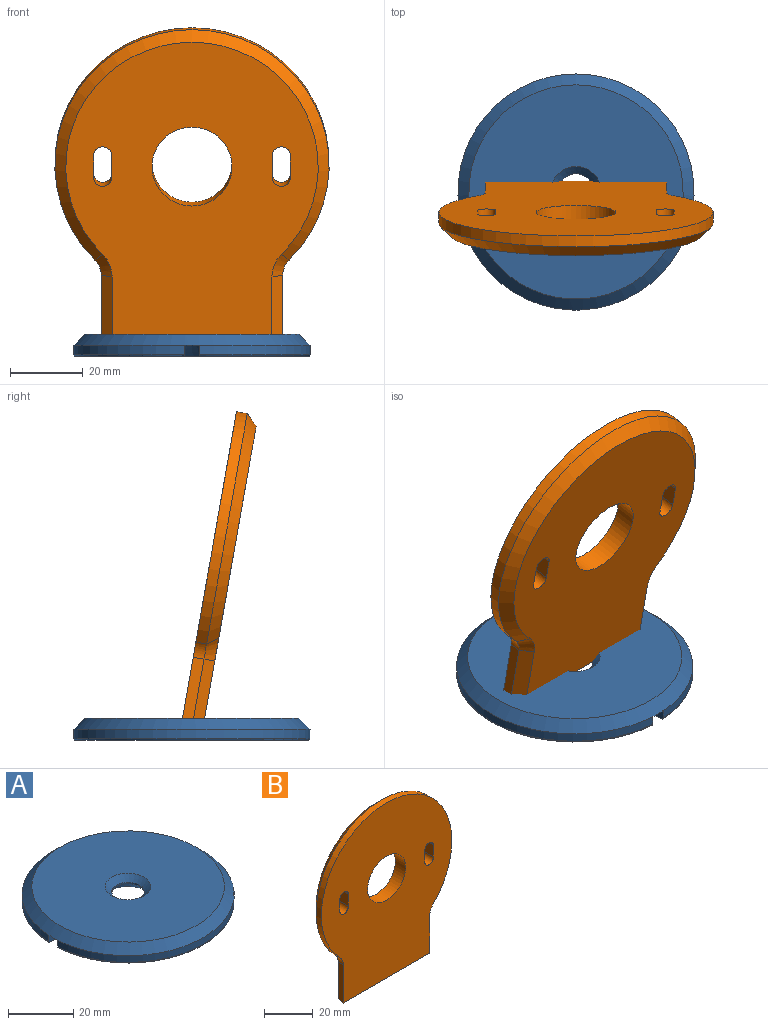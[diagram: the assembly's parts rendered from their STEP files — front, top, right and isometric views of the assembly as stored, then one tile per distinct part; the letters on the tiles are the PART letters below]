
ASSEMBLY  parts=2 mates=1
PART A: 11 faces, bbox 70.5x70.6x6.2 mm
  f0: cylinder r=5mm len=10mm, axis (0,0,-1), area 15.7mm2, adj f8,f9
  f1: plane 64x63.94mm, normal (0,0,-1), area 2895.8mm2, adj f5,f6,f9,f10
  f2: cylinder r=32.5mm len=65mm, axis (0,0,-1), area 500.5mm2, adj f4,f5,f6,f10
  f3: plane 59x59mm, normal (0,0,1), area 2580mm2, adj f4,f8
  f4: cone r=29.5mm half-angle=45deg, axis (0,0,-1), area 826.4mm2, adj f2,f3,f7
  f5: plane 27.52x3.21mm, normal (0,-1,0), area 77.2mm2, adj f1,f2,f7,f9,f10
  f6: plane 27.52x3.21mm, normal (0,1,0), area 77.2mm2, adj f1,f2,f7,f9,f10
  f7: plane 27.38x4mm, normal (0,0,-1), area 108.4mm2, adj f4,f5,f6,f9
  f8: cone r=5mm half-angle=45deg, axis (0,0,1), area 106.6mm2, adj f0,f3
  f9: cone r=8.5mm half-angle=45deg, axis (0,0,-1), area 192.1mm2, adj f0,f1,f5,f6,f7
  f10: torus R=32mm, axis (0,0,1), area 156.3mm2, adj f1,f2,f5,f6
PART B: 22 faces, bbox 75.5x6x87.8 mm
  f0: plane 19.13x3mm, normal (1,0,0), area 56.6mm2, adj f3,f4,f16,f21
  f1: plane 19.13x3mm, normal (-1,0,0), area 56.6mm2, adj f2,f6,f16,f21
  f2: plane 18.6x3mm, normal (-0.71,0.71,0), area 77.8mm2, adj f1,f17,f18,f21
  f3: plane 18.6x3mm, normal (0.71,0.71,0), area 77.8mm2, adj f0,f17,f20,f21
  f4: cylinder r=6mm len=4.23mm, axis (0,1,0), area 14.1mm2, adj f0,f5,f16,f20
  f5: cylinder r=37.75mm len=75.5mm, axis (0,1,0), area 533.2mm2, adj f4,f6,f16,f19
  f6: cylinder r=6mm len=4.23mm, axis (0,1,0), area 14.1mm2, adj f1,f5,f16,f18
  f7: cylinder r=2.5mm len=6mm, axis (0,1,0), area 47.1mm2, adj f8,f13,f16,f17
  f8: plane 6x6mm, normal (-1,0,0), area 36mm2, adj f7,f9,f16,f17
  f9: cylinder r=2.5mm len=6mm, axis (0,1,0), area 47.1mm2, adj f8,f13,f16,f17
  f10: plane 6x6mm, normal (1,0,0), area 36mm2, adj f11,f15,f16,f17
  f11: cylinder r=2.5mm len=6mm, axis (0,1,0), area 47.1mm2, adj f10,f12,f16,f17
  f12: plane 6x6mm, normal (-1,0,0), area 36mm2, adj f11,f15,f16,f17
  f13: plane 6x6mm, normal (1,0,0), area 36mm2, adj f7,f9,f16,f17
  f14: cylinder r=11.01mm len=22.02mm, axis (0,1,0), area 415.1mm2, adj f16,f17
  f15: cylinder r=2.5mm len=6mm, axis (0,1,0), area 47.1mm2, adj f10,f12,f16,f17
  f16: plane 87.75x75.5mm, normal (0,-1,0), area 4759.8mm2, adj f0,f1,f4,f5,f6,f7,f8,f9
  f17: plane 83.69x69.5mm, normal (0,1,0), area 4051.2mm2, adj f2,f3,f7,f8,f9,f10,f11,f12
  f18: cone r=9mm half-angle=45deg, axis (0,1,0), area 24.9mm2, adj f2,f6,f17,f19
  f19: cone r=37.75mm half-angle=45deg, axis (0,-1,0), area 724.1mm2, adj f5,f17,f18,f20
  f20: cone r=9mm half-angle=45deg, axis (0,1,0), area 24.9mm2, adj f3,f4,f17,f19
  f21: plane 50x6mm, normal (0,0.17,-0.98), area 295.5mm2, adj f0,f1,f2,f3,f16,f17
PLACE A rot(axis=(0,0,1),90deg) t=(0,0,0)mm
PLACE B rot(axis=(0,-0.09,1),180deg) t=(0,-2.93,2.96)mm
MATE fastened A.f0 <-> B.f21  axis (0,0,-1) through (0,0,4)mm
